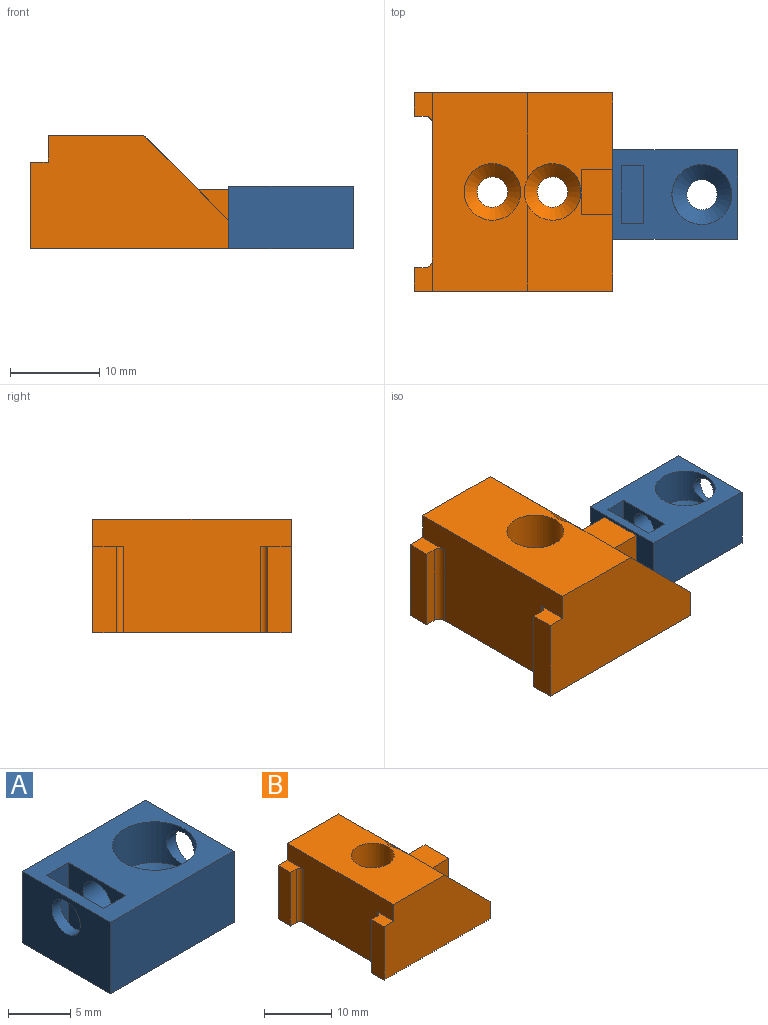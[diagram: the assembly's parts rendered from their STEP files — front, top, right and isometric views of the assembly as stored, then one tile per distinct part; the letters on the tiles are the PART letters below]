
ASSEMBLY  parts=2 mates=2
PART A: 17 faces, bbox 14x10x7 mm
  f0: plane 14x10mm, normal (0,0,1), area 88.3mm2, adj f2,f3,f4,f5,f9,f12,f13,f14
  f1: cylinder r=1.6mm len=3.55mm, axis (1,0,0), area 33.6mm2, adj f9,f13
  f2: plane 10x7mm, normal (-1,0,0), area 62mm2, adj f0,f3,f5,f6,f11
  f3: plane 14x7mm, normal (0,-1,0), area 98mm2, adj f0,f2,f4,f6
  f4: plane 10x7mm, normal (1,0,0), area 62mm2, adj f0,f3,f5,f6,f10
  f5: plane 14x7mm, normal (0,1,0), area 98mm2, adj f0,f2,f4,f6
  f6: plane 14x10mm, normal (0,0,-1), area 130.9mm2, adj f2,f3,f4,f5,f7
  f7: cylinder r=1.7mm len=3.4mm, axis (0,0,1), area 14.3mm2, adj f6,f8
  f8: cone r=1.7mm half-angle=45deg, axis (0,0,1), area 37.3mm2, adj f7,f9
  f9: cylinder r=3.36mm len=6.72mm, axis (0,0,-1), area 67.9mm2, adj f0,f1,f8,f10
  f10: cylinder r=1.6mm len=3.2mm, axis (1,0,0), area 8.4mm2, adj f4,f9
  f11: cylinder r=1.6mm len=3.2mm, axis (1,0,0), area 10.1mm2, adj f2,f12
  f12: plane 6.5x6.5mm, normal (1,0,0), area 34.2mm2, adj f0,f11,f14,f15,f16
  f13: plane 6.5x6.5mm, normal (-1,0,0), area 34.2mm2, adj f0,f1,f14,f15,f16
  f14: plane 6.5x2.5mm, normal (0,-1,0), area 16.2mm2, adj f0,f12,f13,f16
  f15: plane 6.5x2.5mm, normal (0,1,0), area 16.2mm2, adj f0,f12,f13,f16
  f16: plane 6.5x2.5mm, normal (0,0,1), area 16.2mm2, adj f12,f13,f14,f15
PART B: 26 faces, bbox 22.2x22.2x12.7 mm
  f0: plane 22.23x12.7mm, normal (0,-1,0), area 230.9mm2, adj f1,f2,f4,f5,f7,f10,f24
  f1: plane 22.23x10.7mm, normal (0,0,1), area 205.3mm2, adj f0,f2,f6,f10,f13,f14
  f2: plane 22.23x9.53mm, normal (0.71,0,0.71), area 231mm2, adj f0,f1,f5,f6,f13,f21,f22,f23
  f3: plane 9.7x2.61mm, normal (-1,0,0), area 25.3mm2, adj f6,f7,f8,f25
  f4: plane 9.7x2.61mm, normal (-1,0,0), area 25.3mm2, adj f0,f7,f9,f24
  f5: plane 22.23x6.68mm, normal (1,0,0), area 88.1mm2, adj f0,f2,f6,f7,f21,f22,f23
  f6: plane 22.23x12.7mm, normal (0,1,0), area 230.9mm2, adj f1,f2,f3,f5,f7,f10,f25
  f7: plane 22.23x22.23mm, normal (0,0,-1), area 442.1mm2, adj f0,f3,f4,f5,f6,f8,f9,f10
  f8: plane 9.7x1.21mm, normal (0,-1,0), area 11.7mm2, adj f3,f7,f11,f25
  f9: plane 9.7x1.21mm, normal (0,1,0), area 11.7mm2, adj f4,f7,f12,f24
  f10: plane 22.23x12.7mm, normal (-1,0,0), area 216.2mm2, adj f0,f1,f6,f7,f11,f12,f24,f25
  f11: cylinder r=0.79mm len=9.7mm, axis (0,0,-1), area 12.1mm2, adj f7,f8,f10,f25
  f12: cylinder r=0.79mm len=9.7mm, axis (0,0,1), area 12.1mm2, adj f7,f9,f10,f24
  f13: cylinder r=3.17mm len=9.7mm, axis (0,0,1), area 137.2mm2, adj f1,f2,f15
  f14: cylinder r=3.17mm len=9.7mm, axis (0,0,1), area 193.5mm2, adj f1,f18
  f15: plane 6.72x6.72mm, normal (0,0,-1), area 3.8mm2, adj f13,f17
  f16: cylinder r=1.7mm len=3.4mm, axis (0,0,1), area 14.3mm2, adj f7,f17
  f17: cone r=1.7mm half-angle=45deg, axis (0,0,1), area 37.3mm2, adj f15,f16
  f18: plane 6.72x6.72mm, normal (0,0,-1), area 3.8mm2, adj f14,f20
  f19: cylinder r=1.7mm len=3.4mm, axis (0,0,1), area 14.3mm2, adj f7,f20
  f20: cone r=1.7mm half-angle=45deg, axis (0,0,1), area 37.3mm2, adj f18,f19
  f21: plane 5x3.5mm, normal (0,0,1), area 17.5mm2, adj f2,f5,f22,f23
  f22: plane 3.5x3.5mm, normal (0,1,0), area 6.1mm2, adj f2,f5,f21
  f23: plane 3.5x3.5mm, normal (0,-1,0), area 6.1mm2, adj f2,f5,f21
  f24: plane 3.41x2mm, normal (0,0,1), area 5.4mm2, adj f0,f4,f9,f10,f12
  f25: plane 3.41x2mm, normal (0,0,1), area 5.4mm2, adj f3,f6,f8,f10,f11
PLACE A t=(-7.1,6.21,-4.27)mm
PLACE B t=(-29.32,0.38,-4.27)mm fixed
MATE planar B.f7 <-> A.f6  axis (0,0,-1) through (-17.48,11.5,-4.27)mm
MATE planar B.f5 <-> A.f2  axis (1,0,0) through (-7.1,11.5,-2.02)mm
